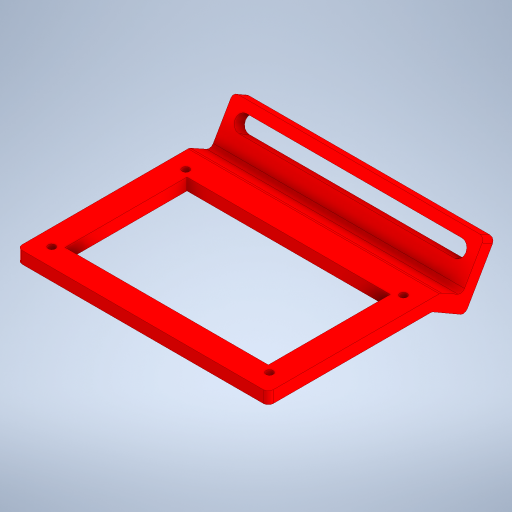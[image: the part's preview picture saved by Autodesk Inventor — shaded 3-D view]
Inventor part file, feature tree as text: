
AUTODESK INVENTOR PART (.ipt)
format: ipt  version: 2023 (Build 270158000, 158)  size: 339,456 bytes
history: native  units: mm
features: extrude x4, fillet x4, sketch x4
ambient origin geometry x8: Origin, YZ Plane, XZ Plane, XY Plane, X Axis, Y Axis, Z Axis, Center Point
bodies: Solid1 (feature_tree)
feature tree (12):
  extrude  "Extrusion1"  Depth=51.0mm
  extrude  "Extrusion2"  Depth=10.0mm
  extrude  "Extrusion3"  Depth=5.0mm TaperAngle=0.0deg
  extrude  "Extrusion4"  Depth=2.0mm
  fillet  "Fillet3"  Radius=3.0mm
  fillet  "Fillet4"  [1 undecoded]
  fillet  "Fillet5"  Radius=13.0mm
  fillet  "Fillet6"  Radius=105.0mm
  sketch  "Sketch1"  dims[d0=85.0mm d1=51.0mm]
  sketch  "Sketch2"  dims[d2=20.0mm d3=10.0mm]
  sketch  "Sketch3"  dims[d4=10.0mm d5=5.0mm d6=0.0mm]
  sketch  "Sketch4"  dims[d13=2.5mm d14=3.0mm d15=3.0mm d16=30.0deg d18=13.0mm d19=105.0mm d20=0.0mm d21=6.5mm d22=90.0mm d23=7.0mm d24=0.0mm d25=0.0mm d26=5.0mm d28=9.0mm d29=0.0mm d30=0.0mm d32=2.0mm d33=45.0mm d34=10.0mm d37=25.0mm d38=2.0mm d39=2.0mm d40=2.0mm]
note: 1 required parameter value undecoded (feature->parameter linkage not recoverable at this tier; creation-order binding heuristic only, values carry confidence <= 0.55)
